# Revit family: SoapDispenser_Wall_Nero_Mecca_Sensor
name_source: partatom
category: Specialty Equipment
units: mm (PartAtom-declared; Revit-internal decimal feet)

## family parameters
Always vertical = Yes
Cut with Voids When Loaded = Yes
Maintain Annotation Orientation = No
OmniClass Number = 23.31.25.29.13
OmniClass Title = Hand Soap Dispensers
Part Type = Normal
Room Calculation Point = No
Round Connector Dimension = Use Diameter
Shared = No
Work Plane-Based = No

## types (6) — shared parameters
Assembly Code = F1040
Default Elevation = 1050 mm
IfcExportAs = IfcFurnitureType
IfcExportType = USERDEFINED
Manufacturer = Nero
ManufacturerOverallDepth = 139 mm  [stored 0.456037 ft]
ManufacturerOverallHeight = 85 mm  [stored 0.278871 ft]
ManufacturerOverallWidth = 60 mm  [stored 0.19685 ft]
ManufacturerURLProductSpecific = https://pleaseloadfromtypecatalog.com
ModifiedIssue = 20251105 $
URL = https://nerotapware.com.au
Uniclass2015Code = Pr_40_70_22_81
Uniclass2015Title = Soap dispensers
Uniclass2015Version = Products v1.35

## per-type parameters (varying)
| type | Description | ManufacturerSpecCode | Material | Model | Type Comments |
| Matte Black (NR408MB) | Mecca Wall Mounted Soap Sensor Dispenser Matte Black | NR408MB | Metal_MatteBlack_Nero | NR408MB | Soap Dispenser - Wall - Sensor - Matte Black |
| Gunmetal (NR408GM) | Mecca Wall Mounted Soap Sensor Dispenser Gun Metal | NR408GM | Metal_GunMetal_Nero | NR408GM | Soap Dispenser - Wall - Sensor - Gunmetal |
| Chrome (NR408CH) | Mecca Wall Mounted Soap Sensor Dispenser Chrome | NR408CH | Metal_Chrome_Nero | NR408CH | Soap Dispenser - Wall - Sensor - Chrome |
| Brushed Bronze (NR408BZ) | Mecca Wall Mounted Soap Sensor Dispenser Brushed Bronze | NR408BZ | Metal_Bronze_Nero_Brushed | NR408BZ | Soap Dispenser - Wall - Sensor - Brushed Bronze |
| Brushed Nickel (NR408BN) | Mecca Wall Mounted Soap Sensor Dispenser Brushed Nickel | NR408BN | Metal_Nickel_Nero_Brushed | NR408BN | Soap Dispenser - Wall - Sensor - Brushed Nickel |
| Brushed Gold (NR408BG) | Mecca Wall Mounted Soap Sensor Dispenser Brushed Gold | NR408BG | Metal_Gold_Nero_Brushed | NR408BG | Soap Dispenser - Wall - Sensor - Brushed Gold |

note: [stored X ft] marks values corroborated as IEEE doubles in the binary element streams (Revit-internal decimal feet)

## geometry (parser evidence)
native form markers: Sweep x2
no freeform markers — native parametric forms only
